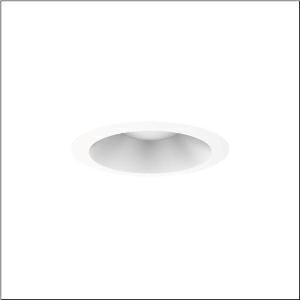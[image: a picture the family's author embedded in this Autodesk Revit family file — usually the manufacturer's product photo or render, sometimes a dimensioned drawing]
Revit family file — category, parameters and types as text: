
# Revit family: lunis_31_midi_51dn15dg32
name_source: partatom
category: Lighting Fixtures
units: mm (PartAtom-declared; Revit-internal decimal feet)

## family parameters
Cut with Voids When Loaded = No
Host = Face
Light Source = No
Part Type = Normal
Room Calculation Point = No
Round Connector Dimension = Use Diameter
Shared = No

## types (1)
- Lunis 31 midi (1 x LED, 2000 lm, 17 W, 3000K)
    Apparent Load = 17 VA
    CIE Flux Codes = 89 99 100 100 100
    Color Rendering = 80
    Color Temperature = 3000K
    Default Elevation = 1800 mm
    Description = Lunis 31,  midi, downlight, light control with lens, light emission: direct distribution, LED rated luminous flux: 2.000lm, light colour: 830, mains connection: 220..240V, AC, 50/60Hz, housing, white, protection rating (complete): IP20, protection rating (on room side): IP54, insulation class (complete): insulation class II (safety insulation), certification: CE, packaging unit: 1 piece
    Height = 0 mm  [stored 0 ft]
    Lamp = 1 x LED
    Lamp Light Flux = 2000 lm
    Lamp Power = 17 W
    Lamp count = 1
    Length = 259 mm
    Luminous efficacy = 118 lm/W
    Manufacturer = Siteco
    ModVariant = No
    Model = 51DN15DG32
    Mounting Place = Ceiling
    Mounting Type = Recessed
    Number of Poles = 1
    OnlyDefault = Yes
    Power Factor = 1
    Product Name = Lunis 31 midi
    Product group = downlight
    ProductGroupID = 400
    Protection Class = Protection class II
    Protection Degree = IP 20
    RLX_Detail_Level = 1
    RLX_Emergency_Light_Flux = 0 lm
    RLX_Emergency_Type = 0
    RLX_Emergency_Type_DB = No
    RlxData = <blob elided: 23629 chars, md5=4e987aa6>
    Socket = socket
    Standby Power = 0 W
    System Light Flux = 2000 lm
    System Power = 17 W
    Type Comments = Product without accessories
    Type Image = l_1006711.jpg
    URL = http://relux.com
    VarID = ---
    Voltage = 0 V
    Weight = 0.00 kg
    Width = 0 mm  [stored 0 ft]

note: [stored X ft] marks values corroborated as IEEE doubles in the binary element streams (Revit-internal decimal feet)

## geometry (parser evidence)
native form markers: Blend x4, Sweep x12
no freeform markers — native parametric forms only
